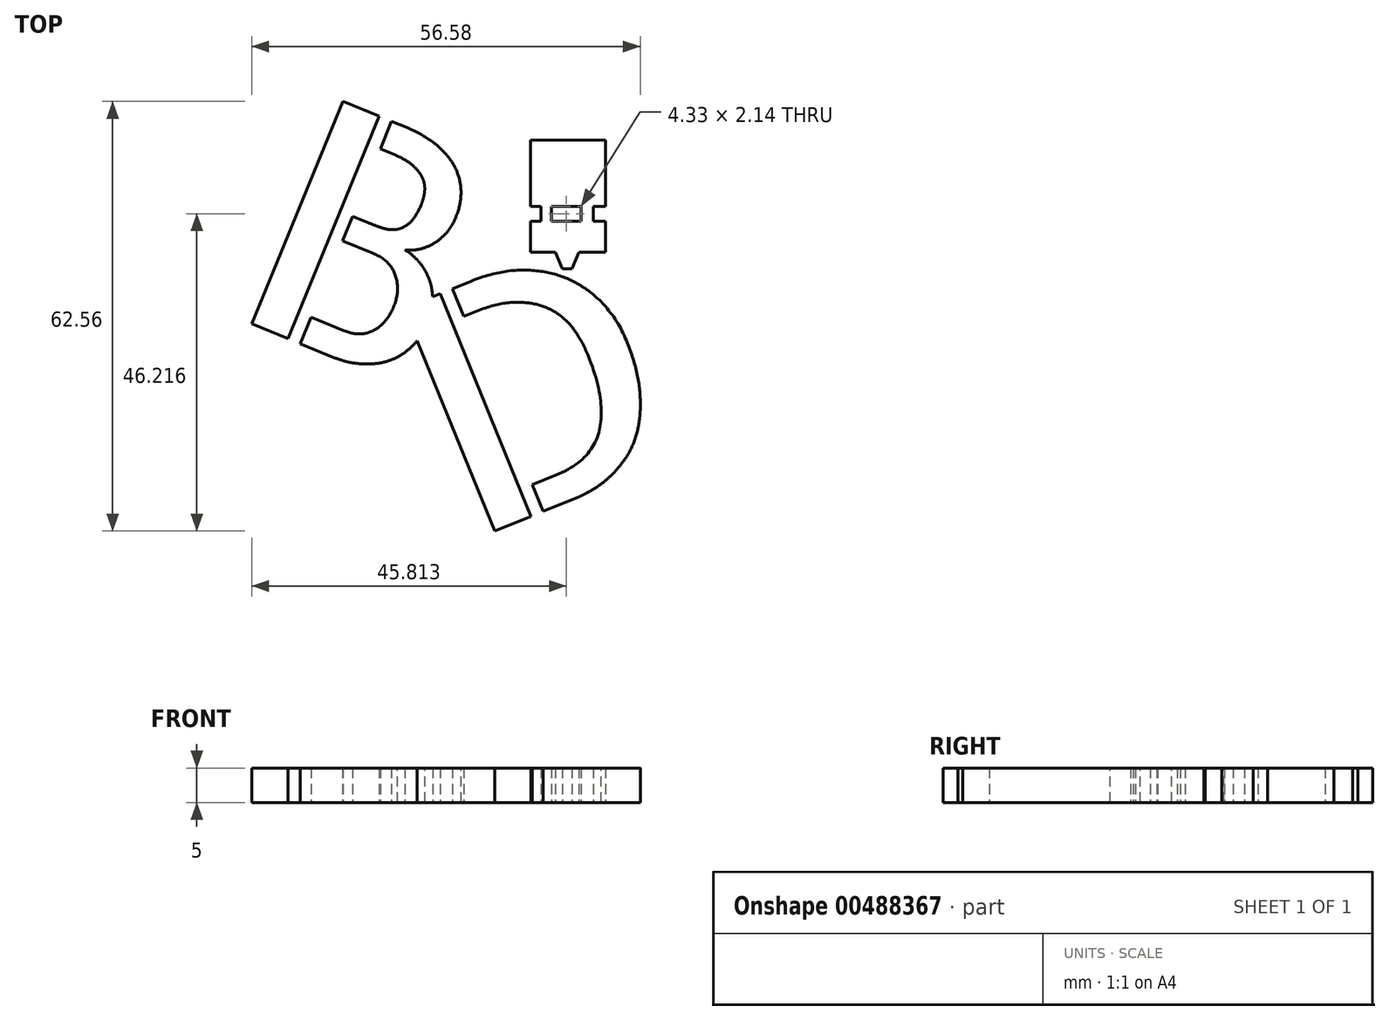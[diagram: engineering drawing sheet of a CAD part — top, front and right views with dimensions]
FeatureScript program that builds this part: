
annotation { "Feature Type Name" : "Feature", "Feature Type Description" : "" }
export const myFeature = defineFeature(function(context is Context, id is Id, definition is map)
    precondition{}
    {
        {
            var Q0;
            Q0=qCreatedBy(makeId("Top.planeOp"),FACE);
            var sketch = newSketch(context, id + "F0", { "sketchPlane" : qUnion([Q0])});
            skText(sketch, "E0", { "text": "B", "fontName": "AllertaStencil-Regular.ttf"});
            skText(sketch, "E1", { "text": "D", "fontName": "AllertaStencil-Regular.ttf"});
            skLineSegment(sketch, "E2.bottom", {"start": v(12.66, 24.98) * mm, "end": v(23.54, 24.98) * mm});
            skLineSegment(sketch, "E2.top", {"start": v(12.66, 15.35) * mm, "end": v(23.54, 15.35) * mm});
            skLineSegment(sketch, "E2.left", {"start": v(12.66, 24.98) * mm, "end": v(12.66, 15.35) * mm});
            skLineSegment(sketch, "E2.right", {"start": v(23.54, 24.98) * mm, "end": v(23.54, 15.35) * mm});
            skLineSegment(sketch, "E3.bottom", {"start": v(12.66, 13.2) * mm, "end": v(23.54, 13.2) * mm});
            skLineSegment(sketch, "E3.top", {"start": v(12.66, 8.64) * mm, "end": v(23.54, 8.64) * mm});
            skLineSegment(sketch, "E3.left", {"start": v(12.66, 13.2) * mm, "end": v(12.66, 8.64) * mm});
            skLineSegment(sketch, "E3.right", {"start": v(23.54, 13.2) * mm, "end": v(23.54, 8.64) * mm});
            skLineSegment(sketch, "E4.bottom", {"start": v(14.14, 15.35) * mm, "end": v(15.69, 15.35) * mm});
            skLineSegment(sketch, "E4.top", {"start": v(14.14, 13.2) * mm, "end": v(15.69, 13.2) * mm});
            skLineSegment(sketch, "E4.left", {"start": v(14.14, 15.35) * mm, "end": v(14.14, 13.2) * mm});
            skLineSegment(sketch, "E4.right", {"start": v(15.69, 15.35) * mm, "end": v(15.69, 13.2) * mm});
            skLineSegment(sketch, "E5.bottom", {"start": v(21.76, 15.35) * mm, "end": v(20.02, 15.35) * mm});
            skLineSegment(sketch, "E5.top", {"start": v(21.76, 13.2) * mm, "end": v(20.02, 13.2) * mm});
            skLineSegment(sketch, "E5.left", {"start": v(21.76, 15.35) * mm, "end": v(21.76, 13.2) * mm});
            skLineSegment(sketch, "E5.right", {"start": v(20.02, 15.35) * mm, "end": v(20.02, 13.2) * mm});
            skLineSegment(sketch, "E6", {"start": v(16.28, 8.64) * mm, "end": v(17.26, 6.24) * mm});
            skLineSegment(sketch, "E7", {"start": v(17.26, 6.24) * mm, "end": v(18.68, 6.24) * mm});
            skLineSegment(sketch, "E8", {"start": v(18.68, 6.24) * mm, "end": v(19.66, 8.64) * mm});
            const initialGuessF0  = {"E0": [-0.03218, 0, 0.9249, -0.3802, 0.035], "E1": [0.00318, -0.03366, 0.92596, 0.37761, 0.035]};
            skSetInitialGuess(sketch, initialGuessF0);
            skSolve(sketch);
        }
        {
            var Q0;
            Q0 = qSketchRegion(id + "F0", true);
            extrude(context, id + "F1", {"entities" : qUnion([Q0]), "depth" : 5 * mm});
        }
    });
